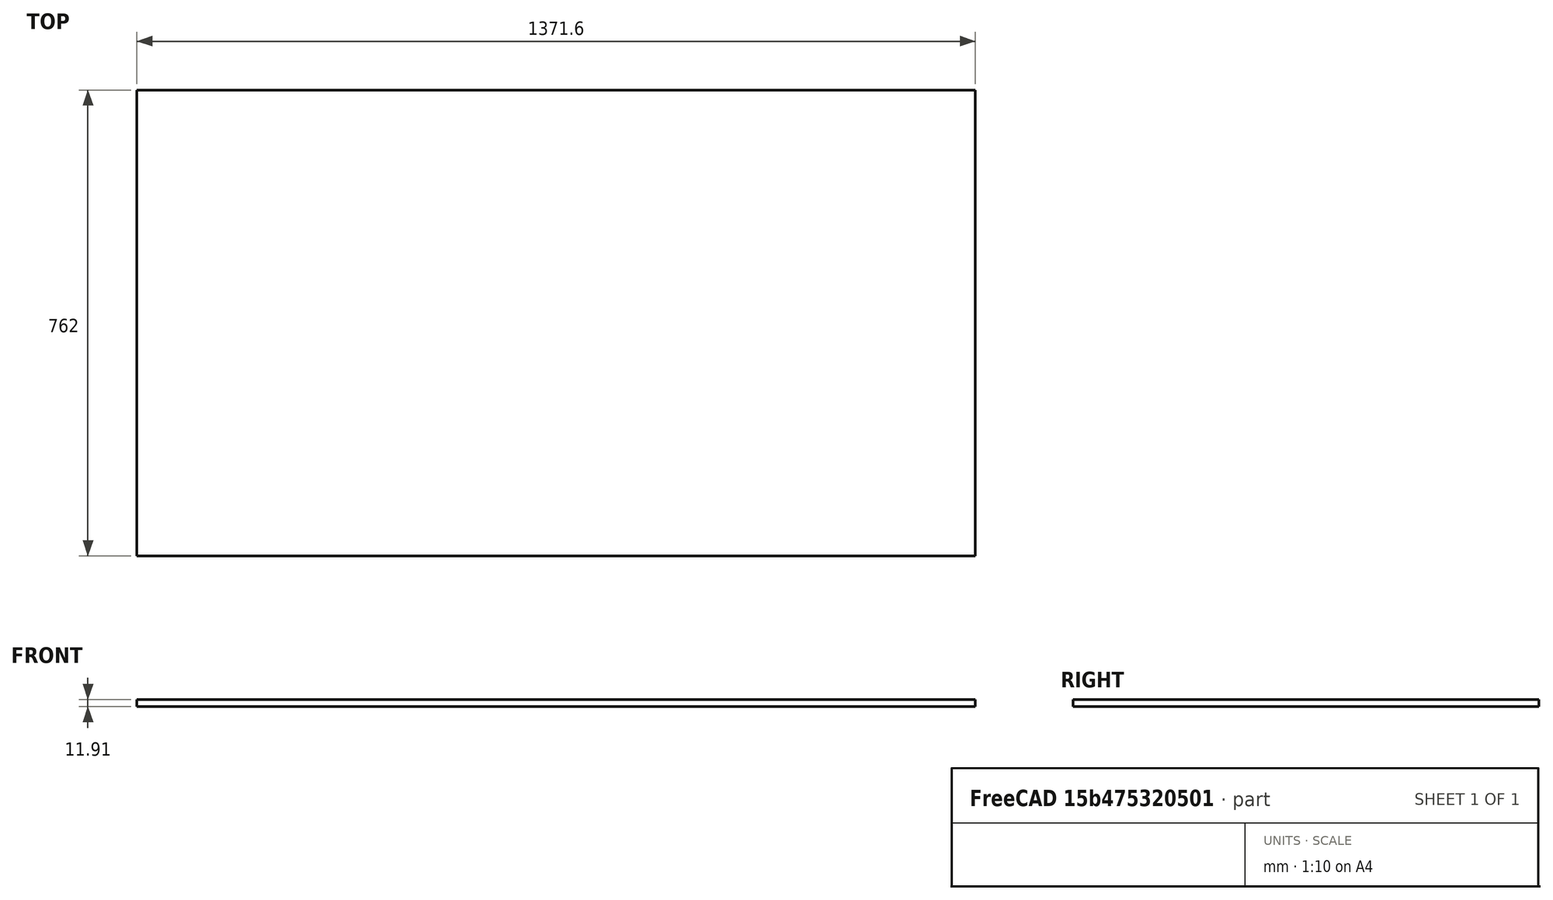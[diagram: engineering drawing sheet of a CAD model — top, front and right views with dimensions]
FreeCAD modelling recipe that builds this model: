
FCSTD DOCUMENT  (FreeCAD 0.20R29603 (Git))
Label: Desktop
License: All rights reserved
LicenseURL: http://en.wikipedia.org/wiki/All_rights_reserved
objects: App::DocumentObjectGroup×3, Sketcher::SketchObject×1, PartDesign::Pad×1, PartDesign::Body×1, PartDesign::CoordinateSystem×1, App::FeaturePython×1, App::Part×1
note: 5 computed .brp shape members not serialized (recipe doc carries the construction recipe); baked Part::Feature solids carry a one-line shape summary decoded from their .brp
EXTERNAL_REF file=Parameters.FCStd obj=Spreadsheet

FEATURE [Sketcher::SketchObject] Sketch
  FullyConstrained = true
  MapMode = 5
  Support = -> [XY_Plane]
  expr: Constraints[8] = <<Parameters>>#<<DeskDimensions>>.Table_Length
  expr: Constraints[9] = <<Parameters>>#<<DeskDimensions>>.Table_Width
  sketch-geometry (4):
    g0: LineSegment StartX=-685.8 StartY=381 StartZ=0 EndX=685.8 EndY=381 EndZ=0
    g1: LineSegment StartX=685.8 StartY=381 StartZ=0 EndX=685.8 EndY=-381 EndZ=0
    g2: LineSegment StartX=685.8 StartY=-381 StartZ=0 EndX=-685.8 EndY=-381 EndZ=0
    g3: LineSegment StartX=-685.8 StartY=-381 StartZ=0 EndX=-685.8 EndY=381 EndZ=0
  constraints (11):
    c: Coincident(g0,g1)
    c: Coincident(g1,g2)
    c: Coincident(g2,g3)
    c: Coincident(g3,g0)
    c: Horizontal(g0)
    c: Horizontal(g2)
    c: Vertical(g1)
    c: Vertical(g3)
    c: DistanceX(g0,g0) = 1371.6
    c: DistanceY(g3,g3) = 762
    c: Symmetric(g0,g1,g-1)
FEATURE [PartDesign::Pad] Pad
  Direction = (0,0,1)
  Length = 11.9062
  Length2 = 10
  Profile = -> Sketch
  ReferenceAxis = -> Sketch [N_Axis]
  Type = 0
  expr: Length = <<Parameters>>#<<DeskDimensions>>.Stock_Thickness
FEATURE [PartDesign::Body] Body
  Group = -> [Sketch,Pad]
  Origin = -> Origin
  Tip = -> Pad
FEATURE [App::DocumentObjectGroup] Parts
FEATURE [PartDesign::CoordinateSystem] LCS_Origin
  AttacherType = Attacher::AttachEngine3D
  MapMode = 2
  Support = -> [X_Axis001]
FEATURE [App::DocumentObjectGroup] Constraints
FEATURE [App::FeaturePython] Variables  # WARN: FeaturePython — macro-defined, semantics opaque (R4)
  Type = App::PropertyContainer
FEATURE [App::DocumentObjectGroup] Configurations
FEATURE [App::Part] Model
  AssemblyType = Part::Link
  Group = -> [LCS_Origin,Constraints,Variables,Configurations,Body]
  Origin = -> Origin001
  SolverId = Asm4EE
  Type = Assembly
